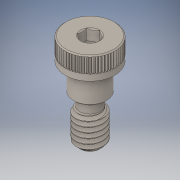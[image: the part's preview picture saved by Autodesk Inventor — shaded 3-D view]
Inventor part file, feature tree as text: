
AUTODESK INVENTOR PART (.ipt)
format: ipt  version: 2019.4 (Build 234330000, 330)  size: 593,408 bytes
history: native  units: in
note: dims shown in document units (in); Inventor stores cm internally (conversion verified against a paired STEP export)
features: chamfer x1
ambient origin geometry x8: Origin, YZ Plane, XZ Plane, XY Plane, X Axis, Y Axis, Z Axis, Center Point
bodies: Solid1 (feature_tree)
feature tree (1):
  chamfer  "Chamfer3"  [1 undecoded]
note: 1 required parameter value undecoded (feature->parameter linkage not recoverable at this tier; creation-order binding heuristic only, values carry confidence <= 0.55)
